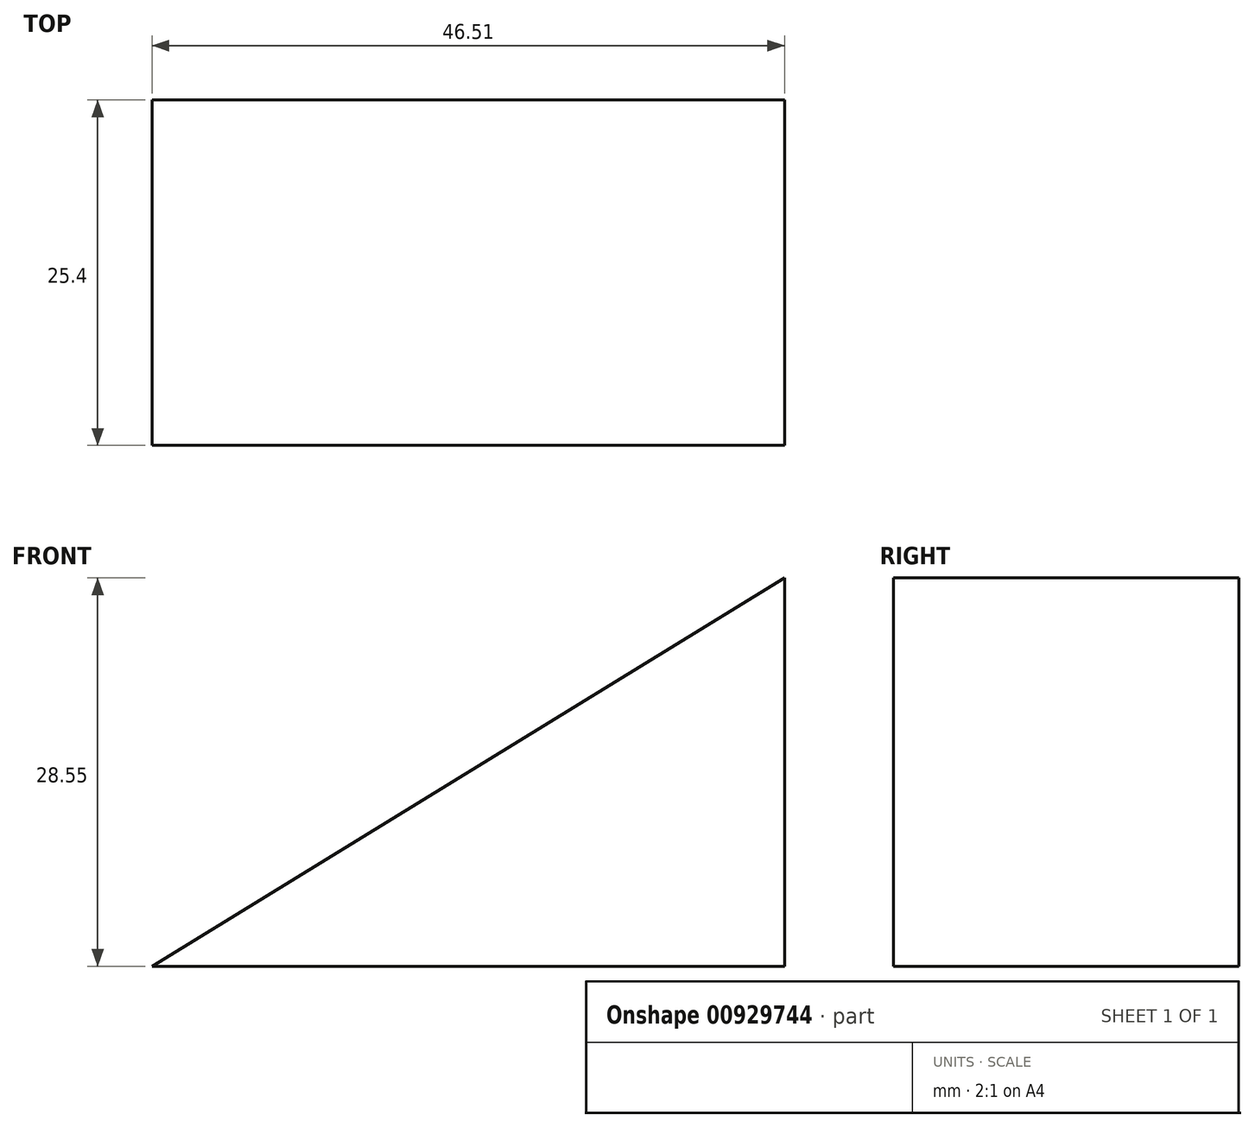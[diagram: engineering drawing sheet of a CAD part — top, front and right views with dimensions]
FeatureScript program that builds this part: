
annotation { "Feature Type Name" : "Feature", "Feature Type Description" : "" }
export const myFeature = defineFeature(function(context is Context, id is Id, definition is map)
    precondition{}
    {
        {
            var Q0;
            Q0=qCreatedBy(makeId("Front.planeOp"),FACE);
            var sketch = newSketch(context, id + "F0", { "sketchPlane" : qUnion([Q0])});
            skLineSegment(sketch, "E0", {"start": v(0, 0) * mm, "end": v(46.51, 28.55) * mm});
            skLineSegment(sketch, "E1", {"start": v(46.51, 28.55) * mm, "end": v(46.51, 0) * mm});
            skLineSegment(sketch, "E2", {"start": v(46.51, 0) * mm, "end": v(0, 0) * mm});
            skSolve(sketch);
        }
        {
            var Q0;
            Q0=makeQuery(id+"F0.imprint","IMPRINT",FACE,{"disambiguationData":[TD([[makeQuery(id+"F0.imprint","IMPRINT",EDGE,{"derivedFrom":sQuery(id+"F0.wireOp",EDGE,"E0")}),-1.0]])]});
            extrude(context, id + "F1", {"entities" : qUnion([Q0]), "depth" : 25.4 * mm, "offsetDistance" : 25.4 * mm});
        }
    });
